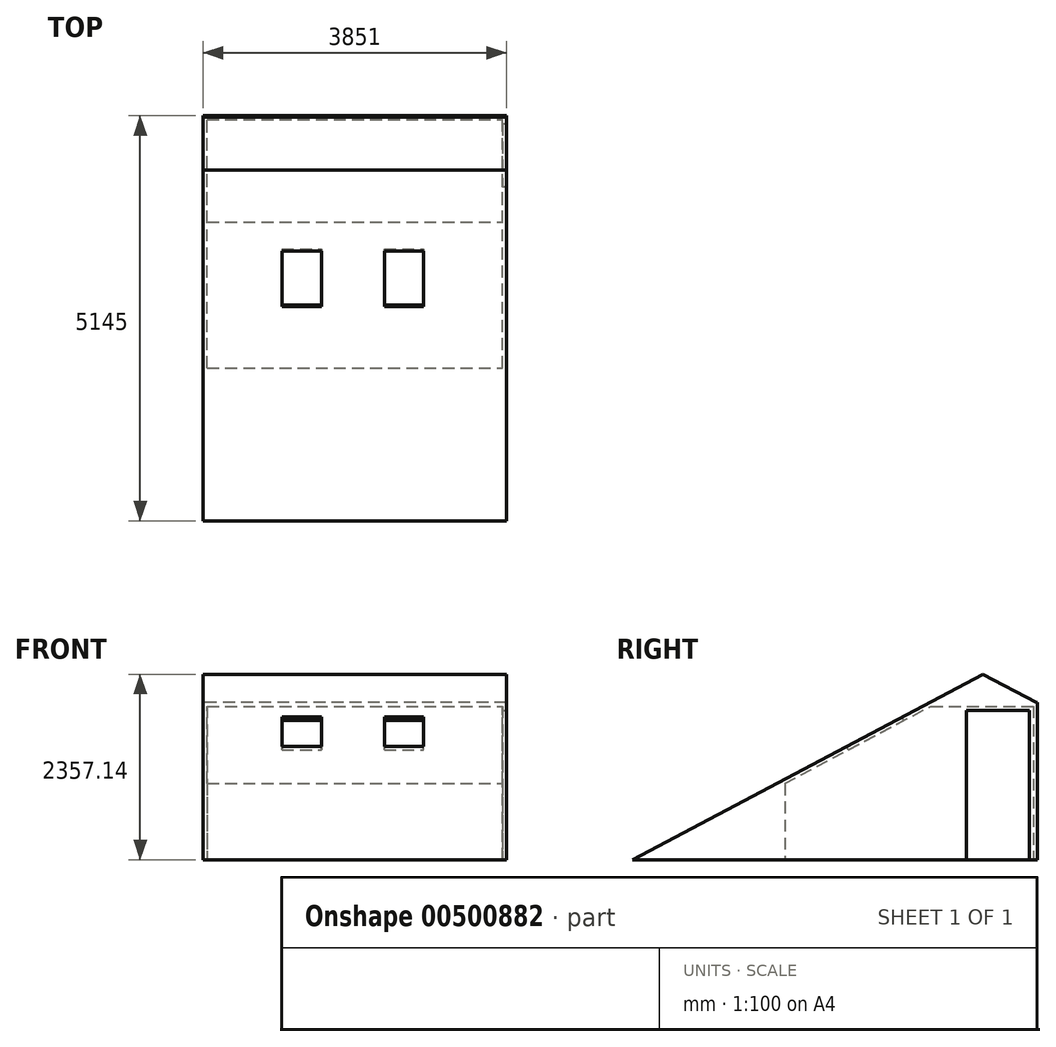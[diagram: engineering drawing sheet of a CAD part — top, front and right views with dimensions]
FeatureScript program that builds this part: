
annotation { "Feature Type Name" : "Feature", "Feature Type Description" : "" }
export const myFeature = defineFeature(function(context is Context, id is Id, definition is map)
    precondition{}
    {
        {
            var Q0;
            Q0=qCreatedBy(makeId("Top.planeOp"),FACE);
            var sketch = newSketch(context, id + "F0", { "sketchPlane" : qUnion([Q0])});
            skLineSegment(sketch, "E0.bottom", {"start": v(0, 0) * mm, "end": v(3851, 0) * mm});
            skLineSegment(sketch, "E0.top", {"start": v(0, 3255) * mm, "end": v(3851, 3255) * mm});
            skLineSegment(sketch, "E0.left", {"start": v(0, 0) * mm, "end": v(0, 3255) * mm});
            skLineSegment(sketch, "E0.right", {"start": v(3851, 0) * mm, "end": v(3851, 3255) * mm});
            skSolve(sketch);
        }
        {
            var Q0;
            Q0 = qSketchRegion(id + "F0", true);
            extrude(context, id + "F1", {"entities" : qUnion([Q0]), "depth" : 2500 * mm});
        }
        {
            var Q0;
            Q0=makeQuery(id+"F1.opExtrude","SWEPT_FACE",FACE,{"disambiguationData":[OSD([sQuery(id+"F0.wireOp",EDGE,"E0.right")])]});
            var sketch = newSketch(context, id + "F2", { "sketchPlane" : qUnion([Q0])});
            skLineSegment(sketch, "E1", {"start": v(0, 1000) * mm, "end": v(1890, 2000) * mm});
            skLineSegment(sketch, "E2", {"start": v(1890, 2000) * mm, "end": v(3255, 2000) * mm});
            skLineSegment(sketch, "E3", {"start": v(3255, 2000) * mm, "end": v(3255, 2500) * mm});
            skLineSegment(sketch, "E4", {"start": v(3255, 2500) * mm, "end": v(0, 2500) * mm});
            skLineSegment(sketch, "E5", {"start": v(0, 2500) * mm, "end": v(0, 1000) * mm});
            skSolve(sketch);
        }
        {
            var Q0;
            Q0 = qSketchRegion(id + "F2", true);
            extrude(context, id + "F3", {"entities" : qUnion([Q0]), "operationType" : NewBodyOperationType.REMOVE, "endBound" : BoundingType.UP_TO_NEXT, "oppositeDirection" : true, "depth" : 25 * mm});
        }
        {
            var Q0;
            Q0=makeQuery(id+"F1.opExtrude","CAP_FACE",FACE,{"disambiguationData":[OSD([sQuery(id+"F0.wireOp",EDGE,"E0.bottom"),sQuery(id+"F0.wireOp",EDGE,"E0.top"),sQuery(id+"F0.wireOp",EDGE,"E0.left"),sQuery(id+"F0.wireOp",EDGE,"E0.right")])],"isStart":true});
            shell(context, id + "F4", {"entities" : qUnion([Q0]), "thickness" : 50 * mm});
        }
        {
            var Q0;
            Q0=makeQuery(id+"F1.opExtrude","SWEPT_FACE",FACE,{"disambiguationData":[OSD([sQuery(id+"F0.wireOp",EDGE,"E0.right")])]});
            var sketch = newSketch(context, id + "F5", { "sketchPlane" : qUnion([Q0])});
            skLineSegment(sketch, "E6.bottom", {"start": v(3155, 0) * mm, "end": v(2355, 0) * mm});
            skLineSegment(sketch, "E6.top", {"start": v(3155, 1900) * mm, "end": v(2355, 1900) * mm});
            skLineSegment(sketch, "E6.left", {"start": v(3155, 0) * mm, "end": v(3155, 1900) * mm});
            skLineSegment(sketch, "E6.right", {"start": v(2355, 0) * mm, "end": v(2355, 1900) * mm});
            skSolve(sketch);
        }
        {
            var Q0;
            Q0 = qSketchRegion(id + "F5", true);
            extrude(context, id + "F6", {"entities" : qUnion([Q0]), "operationType" : NewBodyOperationType.REMOVE, "endBound" : BoundingType.UP_TO_NEXT, "oppositeDirection" : true, "depth" : 25 * mm});
        }
        {
            var Q0;
            Q0=makeQuery(id+"F3.boolean.opBoolean","COPY",FACE,{"derivedFrom":makeQuery(id+"F3.opExtrude","SWEPT_FACE",FACE,{"disambiguationData":[OSD([sQuery(id+"F2.wireOp",EDGE,"E1")])]})});
            var sketch = newSketch(context, id + "F7", { "sketchPlane" : qUnion([Q0])});
            skLineSegment(sketch, "E7.bottom", {"start": v(1000, 2205.92) * mm, "end": v(1500, 2205.92) * mm});
            skLineSegment(sketch, "E7.top", {"start": v(1000, 1405.92) * mm, "end": v(1500, 1405.92) * mm});
            skLineSegment(sketch, "E7.left", {"start": v(1000, 2205.92) * mm, "end": v(1000, 1405.92) * mm});
            skLineSegment(sketch, "E7.right", {"start": v(1500, 2205.92) * mm, "end": v(1500, 1405.92) * mm});
            skLineSegment(sketch, "E8.bottom", {"start": v(2300, 1405.92) * mm, "end": v(2800, 1405.92) * mm});
            skLineSegment(sketch, "E8.top", {"start": v(2300, 2205.92) * mm, "end": v(2800, 2205.92) * mm});
            skLineSegment(sketch, "E8.left", {"start": v(2300, 1405.92) * mm, "end": v(2300, 2205.92) * mm});
            skLineSegment(sketch, "E8.right", {"start": v(2800, 1405.92) * mm, "end": v(2800, 2205.92) * mm});
            skSolve(sketch);
        }
        {
            var Q0;
            Q0 = qSketchRegion(id + "F7", true);
            extrude(context, id + "F8", {"entities" : qUnion([Q0]), "operationType" : NewBodyOperationType.REMOVE, "endBound" : BoundingType.UP_TO_NEXT, "oppositeDirection" : true, "depth" : 25 * mm, "offsetDistance" : 25 * mm});
        }
        {
            var Q0;
            Q0=makeQuery(id+"F1.opExtrude","SWEPT_FACE",FACE,{"disambiguationData":[OSD([sQuery(id+"F0.wireOp",EDGE,"E0.left")])]});
            var sketch = newSketch(context, id + "F9", { "sketchPlane" : qUnion([Q0])});
            skLineSegment(sketch, "E9", {"start": v(-2565, 2357.14) * mm, "end": v(-1890, 2000) * mm});
            skLineSegment(sketch, "E10", {"start": v(0, 0) * mm, "end": v(0, 1000) * mm});
            skLineSegment(sketch, "E11", {"start": v(0, 1000) * mm, "end": v(1890, 0) * mm});
            skLineSegment(sketch, "E12", {"start": v(1890, 0) * mm, "end": v(0, 0) * mm});
            skLineSegment(sketch, "E13", {"start": v(-2565, 2357.14) * mm, "end": v(-3240, 2000) * mm});
            skLineSegment(sketch, "E14", {"start": v(-1890, 2000) * mm, "end": v(-3240, 2000) * mm});
            skSolve(sketch);
        }
        {
            var Q0;
            Q0 = qSketchRegion(id + "F9", true);
            var Q1;
            Q1=makeQuery(id+"F1.opExtrude","SWEPT_FACE",FACE,{"disambiguationData":[OSD([sQuery(id+"F0.wireOp",EDGE,"E0.right")])]});
            extrude(context, id + "F10", {"entities" : qUnion([Q0]), "operationType" : NewBodyOperationType.ADD, "endBound" : BoundingType.UP_TO_SURFACE, "oppositeDirection" : true, "depth" : 25 * mm, "endBoundEntityFace" : qUnion([Q1]), "offsetDistance" : 25 * mm});
        }
    });
